# Revit family: SIENA top fix
name_source: partatom
category: Generic Models
units: mm (PartAtom-declared; Revit-internal decimal feet)

## family parameters
Always vertical = Yes
Can host rebar = No
Cut with Voids When Loaded = No
Part Type = Normal
Room Calculation Point = No
Round Connector Dimension = Use Diameter
Shared = No
Work Plane-Based = No

## types (5) — shared parameters
HEIGHT = 1100 mm
Keynote = UNEX SYSTEMS, SIENA TOP FIX BALUSTRADE
LENGTH = 2500 mm
Manufacturer = UNEX SYSTEMS
Max Post Spacing = 1000 mm  [stored 3.28084 ft]
Pannel QTY = 3
Post QTY = 4
URL = WWW.UNEX.CO.NZ
zero-valued in all types: Default Elevation

## per-type parameters (varying)
| type | ART TOP RAIL | Description | Model | PPR TOP RAIL | Post Height | Top Rail Height | VRE TOP RAIL | VRR TOP RAIL | VRT TOP RAIL |
| SIENA WITH VRE | No | UNEX SIENA FRAMED GLASS WITH VRE TOP RAIL | UNEX,SIENA TOP FIX (VRE) | No | 1080 mm  [stored 3.54331 ft] | 20 mm  [stored 0.0656168 ft] | Yes | No | No |
| SIENA WITH PRR | No | UNEX SIENA FRAMED GLASS WITH PRR TOP RAIL | UNEX, SIENA TOP FIX (PRR) | Yes | 1076 mm  [stored 3.53018 ft] | 24 mm  [stored 0.0787402 ft] | No | No | No |
| SIENA WITH ART | Yes | UNEX SIENA FRAMED GLASS WITH ART TOP RAIL | UNEX, SIENATOP FIX (ART) | No | 1076 mm  [stored 3.53018 ft] | 24 mm  [stored 0.0787402 ft] | No | No | No |
| SIENA WITH VRT | No | UNEX SIENA FRAMED GLASS WITH VRT TOP RAIL | UNEX, SIENA TOP FIX (VRT) | No | 1076 mm  [stored 3.53018 ft] | 24 mm  [stored 0.0787402 ft] | No | No | Yes |
| SIENA WITH VRR | No | UNEX SIENA FRAMED GLASS WITH VRR TOP RAIL | UNEX, SIENA TOP FIX (VRR) | No | 1076 mm  [stored 3.53018 ft] | 24 mm  [stored 0.0787402 ft] | No | Yes | No |

note: [stored X ft] marks values corroborated as IEEE doubles in the binary element streams (Revit-internal decimal feet)

## geometry (parser evidence)
native form markers: Blend x2, Sweep x24
no freeform markers — native parametric forms only
